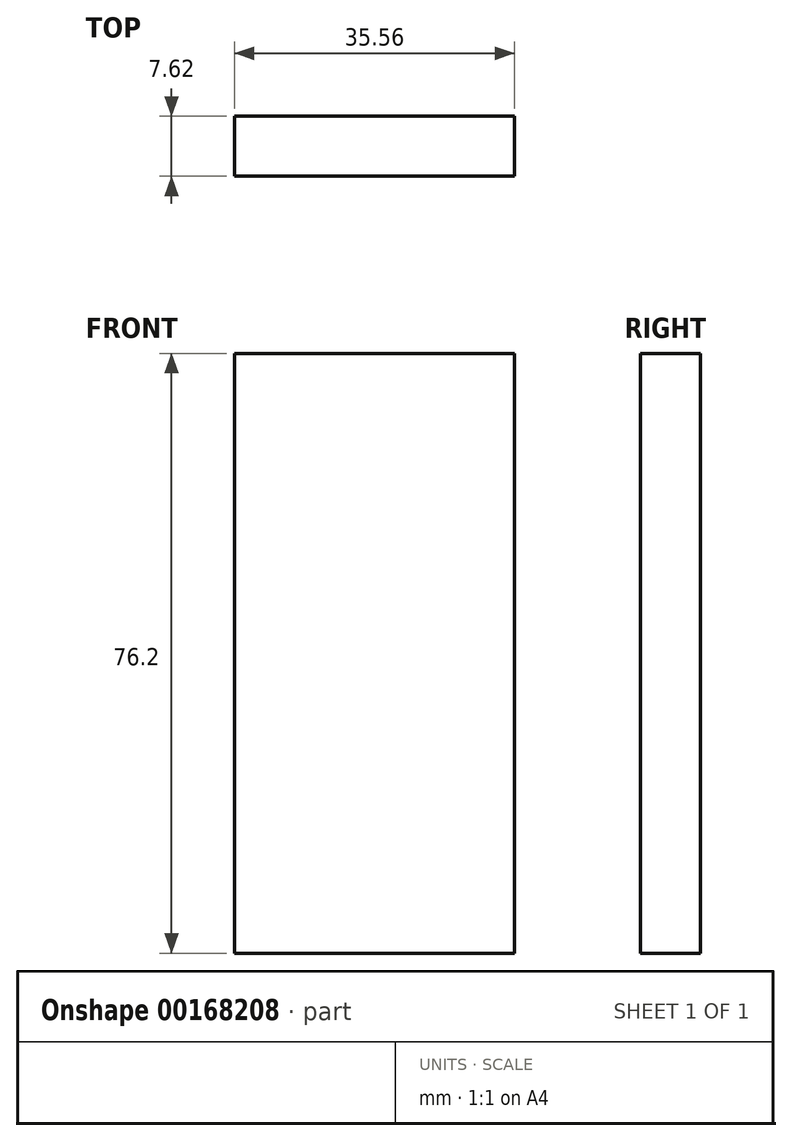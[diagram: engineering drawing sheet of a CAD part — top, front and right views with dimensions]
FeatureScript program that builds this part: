
annotation { "Feature Type Name" : "Feature", "Feature Type Description" : "" }
export const myFeature = defineFeature(function(context is Context, id is Id, definition is map)
    precondition{}
    {
        {
            var Q0;
            Q0=qCreatedBy(makeId("Front.planeOp"),FACE);
            var sketch = newSketch(context, id + "F0", { "sketchPlane" : qUnion([Q0])});
            skLineSegment(sketch, "E0.bottom", {"start": v(17.78, -38.1) * mm, "end": v(-17.78, -38.1) * mm});
            skLineSegment(sketch, "E0.top", {"start": v(17.78, 38.1) * mm, "end": v(-17.78, 38.1) * mm});
            skLineSegment(sketch, "E0.left", {"start": v(17.78, -38.1) * mm, "end": v(17.78, 38.1) * mm});
            skLineSegment(sketch, "E0.right", {"start": v(-17.78, -38.1) * mm, "end": v(-17.78, 38.1) * mm});
            skPoint(sketch, "E0.middle", {"position": v(0, 0) * mm});
            skSolve(sketch);
        }
        {
            var Q0;
            Q0=qSketchRegion(id+"F0",true);
            extrude(context, id + "F1", {"entities" : qUnion([Q0]), "depth" : 7.62 * mm});
        }
    });
